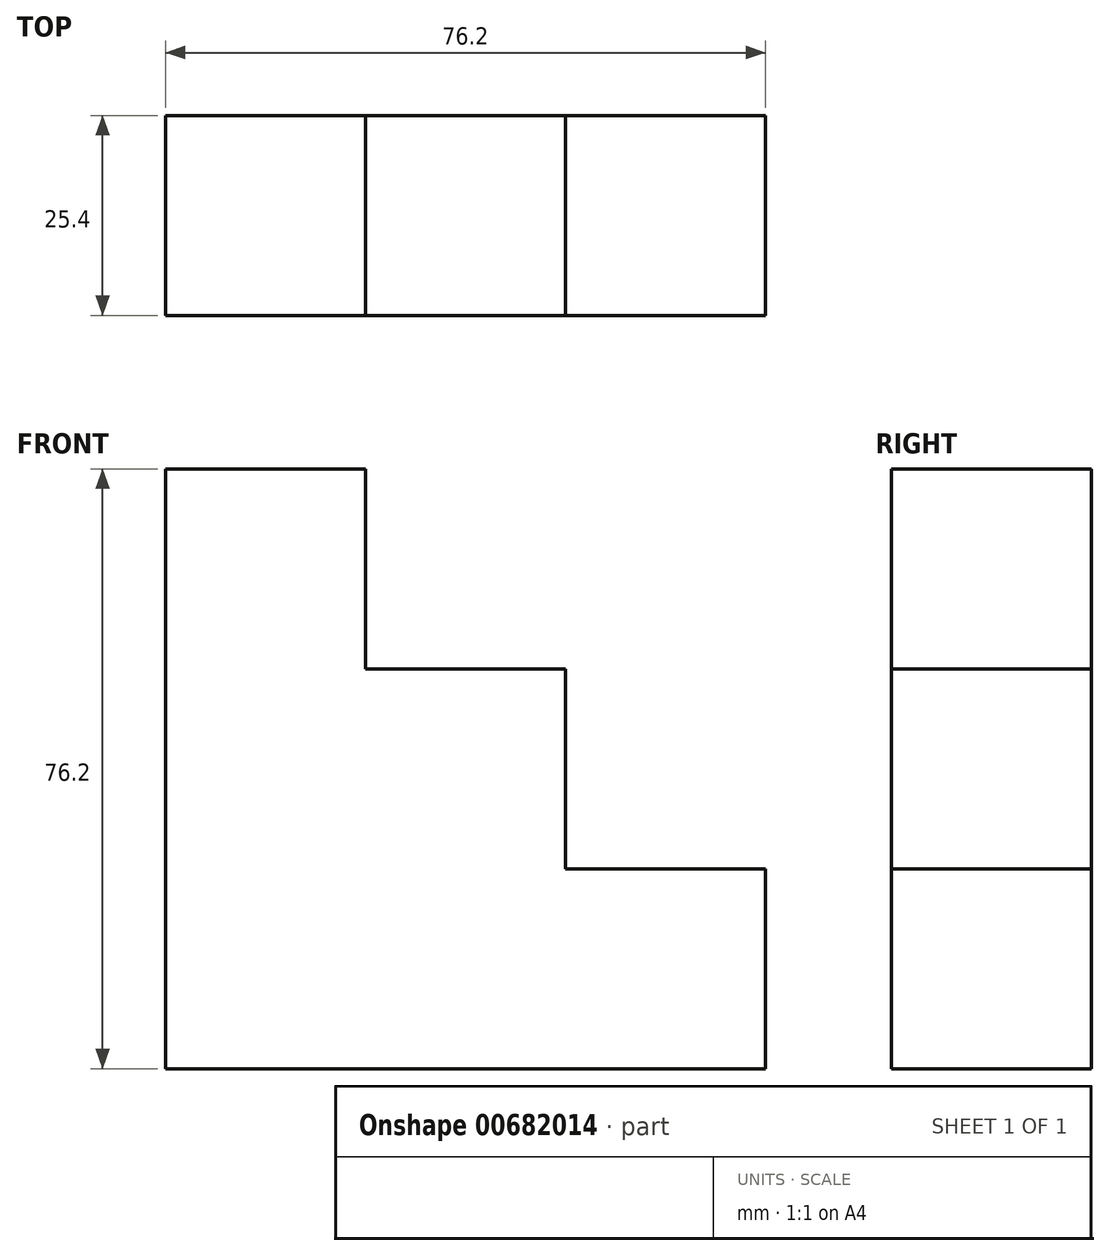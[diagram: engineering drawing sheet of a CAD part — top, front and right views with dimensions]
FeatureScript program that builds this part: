
annotation { "Feature Type Name" : "Feature", "Feature Type Description" : "" }
export const myFeature = defineFeature(function(context is Context, id is Id, definition is map)
    precondition{}
    {
        {
            var Q0;
            Q0=qCreatedBy(makeId("Front.planeOp"),FACE);
            var sketch = newSketch(context, id + "F0", { "sketchPlane" : qUnion([Q0])});
            skLineSegment(sketch, "E0", {"start": v(0, 0) * mm, "end": v(-76.2, 0) * mm});
            skLineSegment(sketch, "E1", {"start": v(-76.2, 0) * mm, "end": v(-76.2, 76.2) * mm});
            skLineSegment(sketch, "E2", {"start": v(-76.2, 76.2) * mm, "end": v(-50.8, 76.2) * mm});
            skLineSegment(sketch, "E3", {"start": v(-50.8, 76.2) * mm, "end": v(-50.8, 50.8) * mm});
            skLineSegment(sketch, "E4", {"start": v(-50.8, 50.8) * mm, "end": v(-25.4, 50.8) * mm});
            skLineSegment(sketch, "E5", {"start": v(-25.4, 50.8) * mm, "end": v(-25.4, 25.4) * mm});
            skLineSegment(sketch, "E6", {"start": v(-25.4, 25.4) * mm, "end": v(0, 25.4) * mm});
            skLineSegment(sketch, "E7", {"start": v(0, 25.4) * mm, "end": v(0, 0) * mm});
            skSolve(sketch);
        }
        {
            var Q0;
            Q0 = qSketchRegion(id + "F0", true);
            extrude(context, id + "F1", {"entities" : qUnion([Q0]), "depth" : 25.4 * mm, "offsetDistance" : 25.4 * mm});
        }
    });
